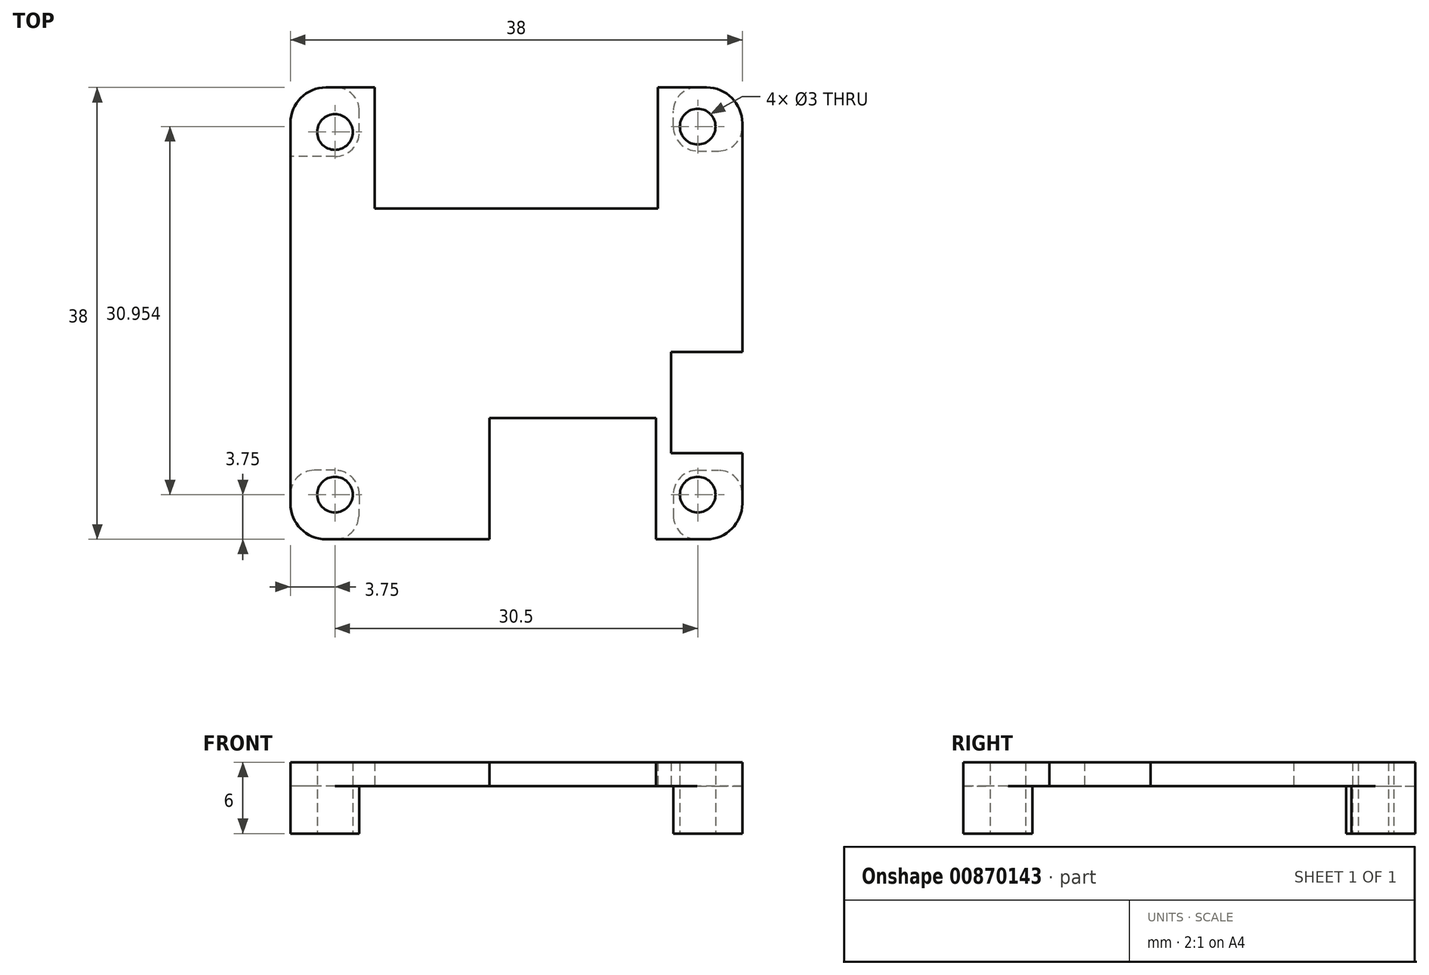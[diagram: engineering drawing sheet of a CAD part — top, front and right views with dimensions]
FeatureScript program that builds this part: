
annotation { "Feature Type Name" : "Feature", "Feature Type Description" : "" }
export const myFeature = defineFeature(function(context is Context, id is Id, definition is map)
    precondition{}
    {
        {
            var Q0;
            Q0=qCreatedBy(makeId("Top.planeOp"),FACE);
            var sketch = newSketch(context, id + "F0", { "sketchPlane" : qUnion([Q0])});
            skLineSegment(sketch, "E0.bottom", {"start": v(16, -19) * mm, "end": v(11.75, -19) * mm});
            skLineSegment(sketch, "E0.top", {"start": v(16, 19) * mm, "end": v(11.9, 19) * mm});
            skLineSegment(sketch, "E0.left", {"start": v(19, -16) * mm, "end": v(19, -11.75) * mm});
            skLineSegment(sketch, "E0.right", {"start": v(-19, -16) * mm, "end": v(-19, 16) * mm});
            skPoint(sketch, "E0.middle", {"position": v(0, 0) * mm});
            skPoint(sketch, "E1", {"position": v(15.25, 15.7) * mm});
            skPoint(sketch, "E2", {"position": v(15.25, -15.25) * mm});
            skPoint(sketch, "E3", {"position": v(-15.25, -15.25) * mm});
            skPoint(sketch, "E4", {"position": v(-15.25, 15.25) * mm});
            skCircle(sketch, "E5", {"center": v(-15.25, 15.25) * mm, "radius": 1.5 * mm});
            skCircle(sketch, "E6", {"center": v(15.25, 15.7) * mm, "radius": 1.5 * mm});
            skCircle(sketch, "E7", {"center": v(15.25, -15.25) * mm, "radius": 1.5 * mm});
            skCircle(sketch, "E8", {"center": v(-15.25, -15.25) * mm, "radius": 1.5 * mm});
            skArc(sketch, "E9", {"start": v(-15.25, 13.2) * mm, "mid": v(-13.8, 13.8) * mm, "end": v(-13.2, 15.25) * mm});
            skArc(sketch, "E10", {"start": v(13.2, 15.7) * mm, "mid": v(13.8, 14.25) * mm, "end": v(15.25, 13.65) * mm});
            skArc(sketch, "E11", {"start": v(-13.2, -15.3) * mm, "mid": v(-13.78, -13.82) * mm, "end": v(-15.25, -13.2) * mm});
            skArc(sketch, "E12", {"start": v(15.25, -13.2) * mm, "mid": v(13.8, -13.8) * mm, "end": v(13.2, -15.25) * mm});
            skLineSegment(sketch, "E13", {"start": v(-15.25, 13.2) * mm, "end": v(-19, 13.2) * mm});
            skLineSegment(sketch, "E14", {"start": v(-13.2, 15.25) * mm, "end": v(-13.2, 19) * mm});
            skLineSegment(sketch, "E15", {"start": v(15.25, 13.65) * mm, "end": v(19, 13.65) * mm});
            skLineSegment(sketch, "E16", {"start": v(13.2, 15.7) * mm, "end": v(13.2, 19) * mm});
            skLineSegment(sketch, "E17", {"start": v(-15.25, -13.2) * mm, "end": v(-19, -13.2) * mm});
            skLineSegment(sketch, "E18", {"start": v(-13.2, -15.3) * mm, "end": v(-13.3, -19) * mm});
            skLineSegment(sketch, "E19", {"start": v(15.25, -13.2) * mm, "end": v(19, -13.2) * mm});
            skLineSegment(sketch, "E20", {"start": v(13.2, -15.25) * mm, "end": v(13.2, -19) * mm});
            skPoint(sketch, "E21.visualSharp", {"position": v(-19, 19) * mm});
            skArc(sketch, "E21.filletArc", {"start": v(-16, 19) * mm, "mid": v(-18.12, 18.12) * mm, "end": v(-19, 16) * mm});
            skPoint(sketch, "E22.visualSharp", {"position": v(19, 19) * mm});
            skArc(sketch, "E22.filletArc", {"start": v(19, 16) * mm, "mid": v(18.12, 18.12) * mm, "end": v(16, 19) * mm});
            skPoint(sketch, "E23.visualSharp", {"position": v(19, -19) * mm});
            skArc(sketch, "E23.filletArc", {"start": v(16, -19) * mm, "mid": v(18.12, -18.12) * mm, "end": v(19, -16) * mm});
            skPoint(sketch, "E24.visualSharp", {"position": v(-19, -19) * mm});
            skArc(sketch, "E24.filletArc", {"start": v(-19, -16) * mm, "mid": v(-18.12, -18.12) * mm, "end": v(-16, -19) * mm});
            skLineSegment(sketch, "E25", {"start": v(0, 8.8) * mm, "end": v(11.9, 8.8) * mm});
            skLineSegment(sketch, "E26", {"start": v(0, 8.8) * mm, "end": v(-11.9, 8.8) * mm});
            skLineSegment(sketch, "E27", {"start": v(-11.9, 8.8) * mm, "end": v(-11.9, 19) * mm});
            skLineSegment(sketch, "E28", {"start": v(11.9, 8.8) * mm, "end": v(11.9, 19) * mm});
            skLineSegment(sketch, "E29.top", {"start": v(11.75, -8.8) * mm, "end": v(-2.25, -8.8) * mm});
            skLineSegment(sketch, "E29.left", {"start": v(11.75, -19) * mm, "end": v(11.75, -8.8) * mm});
            skLineSegment(sketch, "E29.right", {"start": v(-2.25, -19) * mm, "end": v(-2.25, -8.8) * mm});
            skLineSegment(sketch, "E30.bottom", {"start": v(19, -11.75) * mm, "end": v(13, -11.75) * mm});
            skLineSegment(sketch, "E30.top", {"start": v(19, -3.25) * mm, "end": v(13, -3.25) * mm});
            skLineSegment(sketch, "E30.right", {"start": v(13, -11.75) * mm, "end": v(13, -3.25) * mm});
            skLineSegment(sketch, "E31.trimOffspring", {"start": v(-11.9, 19) * mm, "end": v(-16, 19) * mm});
            skLineSegment(sketch, "E32.trimOffspring", {"start": v(-2.25, -19) * mm, "end": v(-16, -19) * mm});
            skLineSegment(sketch, "E33.trimOffspring", {"start": v(19, -3.25) * mm, "end": v(19, 16) * mm});
            skSolve(sketch);
        }
        {
            var Q0;
            Q0=makeQuery(id+"F0.imprint","IMPRINT",FACE,{"disambiguationData":[TD([[makeQuery(id+"F0.imprint","IMPRINT",EDGE,{"derivedFrom":sQuery(id+"F0.wireOp",EDGE,"E9")}),-1.0]])]});
            var Q1;
            Q1=makeQuery(id+"F0.imprint","IMPRINT",FACE,{"disambiguationData":[TD([[makeQuery(id+"F0.imprint","IMPRINT",EDGE,{"derivedFrom":sQuery(id+"F0.wireOp",EDGE,"E5")}),-1.0]])]});
            var Q2;
            Q2=makeQuery(id+"F0.imprint","IMPRINT",FACE,{"disambiguationData":[TD([[makeQuery(id+"F0.imprint","IMPRINT",EDGE,{"derivedFrom":sQuery(id+"F0.wireOp",EDGE,"E6")}),-1.0]])]});
            var Q3;
            Q3=makeQuery(id+"F0.imprint","IMPRINT",FACE,{"disambiguationData":[TD([[makeQuery(id+"F0.imprint","IMPRINT",EDGE,{"derivedFrom":sQuery(id+"F0.wireOp",EDGE,"E7")}),-1.0]])]});
            var Q4;
            Q4=makeQuery(id+"F0.imprint","IMPRINT",FACE,{"disambiguationData":[TD([[makeQuery(id+"F0.imprint","IMPRINT",EDGE,{"derivedFrom":sQuery(id+"F0.wireOp",EDGE,"E8")}),-1.0]])]});
            extrude(context, id + "F1", {"entities" : qUnion([Q0, Q1, Q2, Q3, Q4]), "depth" : 2 * mm, "offsetDistance" : 25 * mm});
        }
        {
            var Q0;
            Q0=makeQuery(id+"F0.imprint","IMPRINT",FACE,{"disambiguationData":[TD([[makeQuery(id+"F0.imprint","IMPRINT",EDGE,{"derivedFrom":sQuery(id+"F0.wireOp",EDGE,"E8")}),-1.0]])]});
            var Q1;
            Q1=makeQuery(id+"F0.imprint","IMPRINT",FACE,{"disambiguationData":[TD([[makeQuery(id+"F0.imprint","IMPRINT",EDGE,{"derivedFrom":sQuery(id+"F0.wireOp",EDGE,"E7")}),-1.0]])]});
            var Q2;
            Q2=makeQuery(id+"F0.imprint","IMPRINT",FACE,{"disambiguationData":[TD([[makeQuery(id+"F0.imprint","IMPRINT",EDGE,{"derivedFrom":sQuery(id+"F0.wireOp",EDGE,"E6")}),-1.0]])]});
            var Q3;
            Q3=makeQuery(id+"F0.imprint","IMPRINT",FACE,{"disambiguationData":[TD([[makeQuery(id+"F0.imprint","IMPRINT",EDGE,{"derivedFrom":sQuery(id+"F0.wireOp",EDGE,"E5")}),-1.0]])]});
            extrude(context, id + "F2", {"entities" : qUnion([Q0, Q1, Q2, Q3]), "operationType" : NewBodyOperationType.ADD, "oppositeDirection" : true, "depth" : 4 * mm, "offsetDistance" : 25 * mm});
        }
        {
            var Q0;
            Q0=makeQuery(id+"F2.opExtrude","SWEPT_EDGE",EDGE,{"disambiguationData":[OSD([sQuery(id+"F0.wireOp",EDGE,"E14"),sQuery(id+"F0.wireOp",EDGE,"E31.trimOffspring")])]});
            fillet(context, id + "F3", {"entities" : qUnion([Q0]), "radius" : 2 * mm, "tangentPropagation" : true, "allowEdgeOverflow" : false});
        }
        {
            var Q0;
            Q0=makeQuery(id+"F2.opExtrude","SWEPT_EDGE",EDGE,{"disambiguationData":[OSD([sQuery(id+"F0.wireOp",EDGE,"E0.top"),sQuery(id+"F0.wireOp",EDGE,"E16")])]});
            var Q1;
            Q1=makeQuery(id+"F2.opExtrude","SWEPT_EDGE",EDGE,{"disambiguationData":[OSD([sQuery(id+"F0.wireOp",EDGE,"E15"),sQuery(id+"F0.wireOp",EDGE,"E33.trimOffspring")])]});
            var Q2;
            Q2=makeQuery(id+"F2.opExtrude","SWEPT_EDGE",EDGE,{"disambiguationData":[OSD([sQuery(id+"F0.wireOp",EDGE,"E0.left"),sQuery(id+"F0.wireOp",EDGE,"E19")])]});
            var Q3;
            Q3=makeQuery(id+"F2.opExtrude","SWEPT_EDGE",EDGE,{"disambiguationData":[OSD([sQuery(id+"F0.wireOp",EDGE,"E0.bottom"),sQuery(id+"F0.wireOp",EDGE,"E20")])]});
            var Q4;
            Q4=makeQuery(id+"F2.opExtrude","SWEPT_EDGE",EDGE,{"disambiguationData":[OSD([sQuery(id+"F0.wireOp",EDGE,"E18"),sQuery(id+"F0.wireOp",EDGE,"E32.trimOffspring")])]});
            var Q5;
            Q5=makeQuery(id+"F2.opExtrude","SWEPT_EDGE",EDGE,{"disambiguationData":[OSD([sQuery(id+"F0.wireOp",EDGE,"E0.right"),sQuery(id+"F0.wireOp",EDGE,"E17")])]});
            fillet(context, id + "F4", {"entities" : qUnion([Q0, Q1, Q2, Q3, Q4, Q5]), "radius" : 2 * mm, "tangentPropagation" : true, "allowEdgeOverflow" : false});
        }
    });
